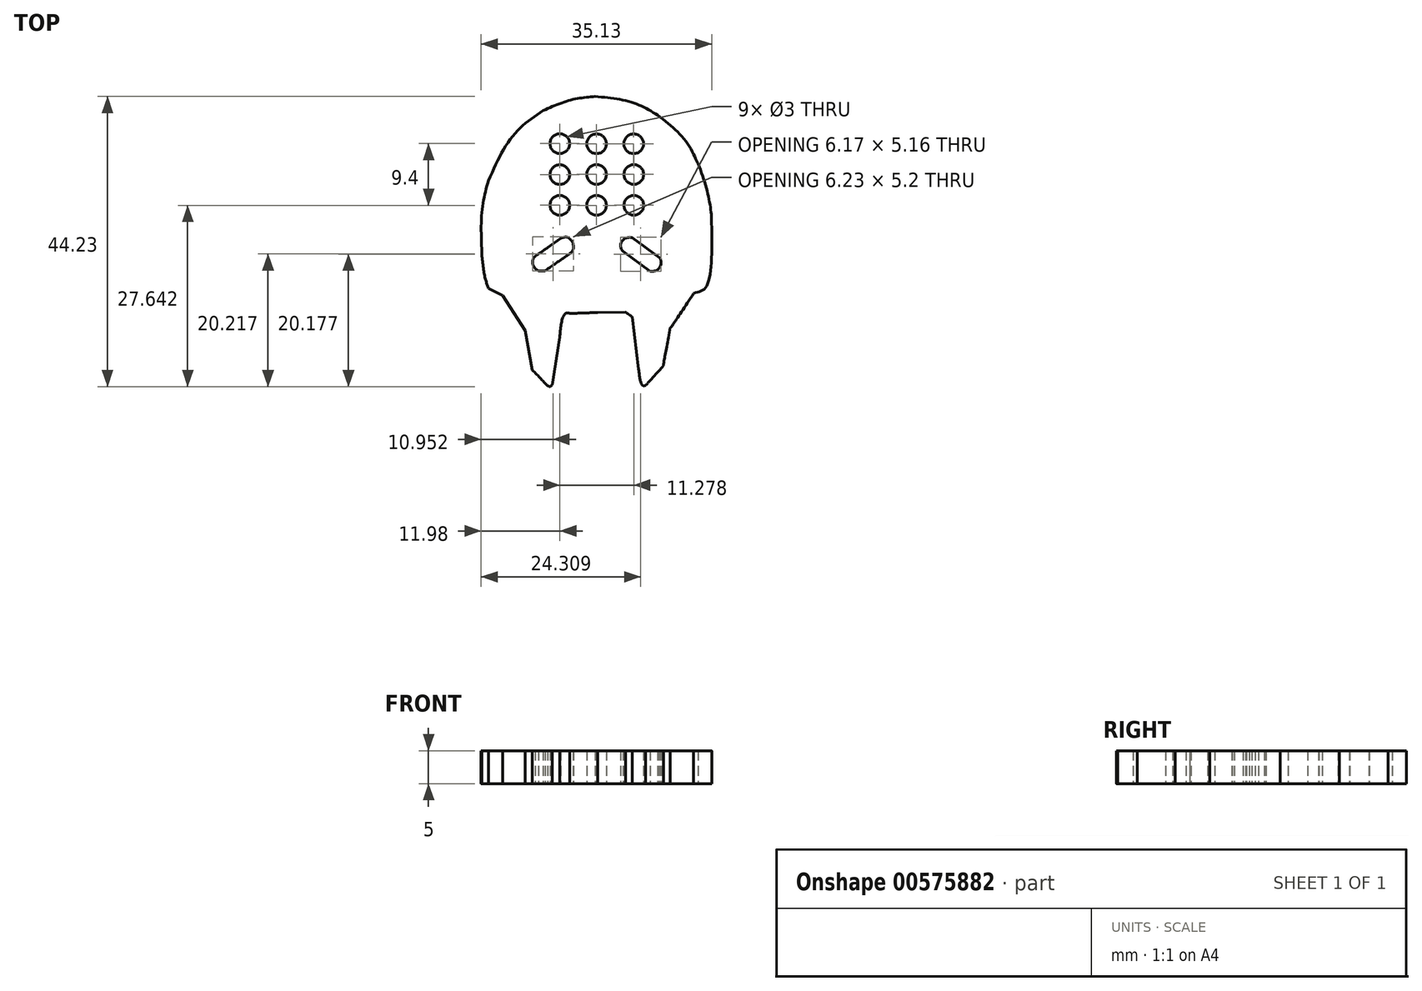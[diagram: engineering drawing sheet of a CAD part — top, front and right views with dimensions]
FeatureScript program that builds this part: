
annotation { "Feature Type Name" : "Feature", "Feature Type Description" : "" }
export const myFeature = defineFeature(function(context is Context, id is Id, definition is map)
    precondition{}
    {
        {
            var Q0;
            Q0=qCreatedBy(makeId("Top.planeOp"),FACE);
            var sketch = newSketch(context, id + "F0", { "sketchPlane" : qUnion([Q0])});
            skFitSpline(sketch, "E0", {"points": [v(28.78, 16.5) * mm, v(24.5, 16.4) * mm], "startDerivative": vector(-4.28, 0) * mm, "endDerivative": vector(-4.28, 0) * mm});
            skFitSpline(sketch, "E1", {"points": [v(24.5, 16.4) * mm, v(23.89, 16.4) * mm, v(23.3, 15.2) * mm, v(22.98, 12.74) * mm], "startDerivative": vector(-3.34, 0.8) * mm, "endDerivative": vector(-0.63, -5.77) * mm});
            skFitSpline(sketch, "E2", {"points": [v(22.98, 12.74) * mm, v(21.82, 5.46) * mm], "startDerivative": vector(-1.15, -7.27) * mm, "endDerivative": vector(-1.15, -7.27) * mm});
            skFitSpline(sketch, "E3", {"points": [v(21.82, 5.46) * mm, v(21.46, 5.22) * mm, v(20.6, 5.93) * mm, v(18.83, 7.75) * mm], "startDerivative": vector(-1.7, -1.87) * mm, "endDerivative": vector(-3.91, 3.94) * mm});
            skFitSpline(sketch, "E4", {"points": [v(18.83, 7.75) * mm, v(17.7, 13.77) * mm], "startDerivative": vector(-1.13, 6.02) * mm, "endDerivative": vector(-1.13, 6.02) * mm});
            skFitSpline(sketch, "E5", {"points": [v(17.7, 13.77) * mm, v(14.28, 19.1) * mm], "startDerivative": vector(-3.42, 5.33) * mm, "endDerivative": vector(-3.42, 5.33) * mm});
            skFitSpline(sketch, "E6", {"points": [v(14.28, 19.1) * mm, v(12.13, 20.22) * mm], "startDerivative": vector(-2.15, 1.12) * mm, "endDerivative": vector(-2.15, 1.12) * mm});
            skFitSpline(sketch, "E7", {"points": [v(12.13, 20.22) * mm, v(11.6, 21.9) * mm, v(11.15, 25.07) * mm], "startDerivative": vector(-1.33, 3.6) * mm, "endDerivative": vector(-0.65, 5.98) * mm});
            skFitSpline(sketch, "E8", {"points": [v(11.15, 25.07) * mm, v(11.15, 32.1) * mm, v(12.13, 36.62) * mm], "startDerivative": vector(-0.6, 13.45) * mm, "endDerivative": vector(2.66, 9.51) * mm});
            skFitSpline(sketch, "E9", {"points": [v(12.13, 36.62) * mm, v(15.93, 43.55) * mm, v(20.45, 47.3) * mm], "startDerivative": vector(6.36, 14.19) * mm, "endDerivative": vector(10.4, 6.99) * mm});
            skFitSpline(sketch, "E10", {"points": [v(20.45, 47.3) * mm, v(24.7, 48.92) * mm, v(28.38, 49.45) * mm], "startDerivative": vector(8.18, 3.62) * mm, "endDerivative": vector(7.66, 0.63) * mm});
            skFitSpline(sketch, "E11", {"points": [v(28.38, 49.45) * mm, v(33.98, 48.57) * mm, v(37.93, 46.6) * mm], "startDerivative": vector(11.1, -0.97) * mm, "endDerivative": vector(7.93, -4.81) * mm});
            skFitSpline(sketch, "E12", {"points": [v(37.93, 46.6) * mm, v(42.66, 42) * mm, v(44.08, 39.22) * mm, v(44.13, 39.22) * mm], "startDerivative": vector(9.54, -7.46) * mm, "endDerivative": vector(0.91, 0.43) * mm});
            skFitSpline(sketch, "E13", {"points": [v(44.08, 39.22) * mm, v(45.88, 33.07) * mm, v(46.13, 30.17) * mm], "startDerivative": vector(4.32, -11.02) * mm, "endDerivative": vector(-0.2, -4) * mm});
            skFitSpline(sketch, "E14", {"points": [v(46.13, 30.17) * mm, v(45.26, 20.37) * mm, v(43.4, 19.44) * mm], "startDerivative": vector(0.3, -18.19) * mm, "endDerivative": vector(-6.92, -2.62) * mm});
            skFitSpline(sketch, "E15", {"points": [v(43.4, 19.44) * mm, v(39.86, 14.17) * mm, v(39.86, 14.2) * mm], "startDerivative": vector(-5.55, -8.44) * mm, "endDerivative": vector(0.11, 0.6) * mm});
            skFitSpline(sketch, "E16", {"points": [v(39.86, 14.2) * mm, v(38.8, 8.42) * mm, v(38.83, 8.44) * mm], "startDerivative": vector(-1.82, -9.27) * mm, "endDerivative": vector(0.4, 0.58) * mm});
            skFitSpline(sketch, "E17", {"points": [v(38.8, 8.42) * mm, v(36.1, 5.42) * mm, v(36.13, 5.44) * mm], "startDerivative": vector(-4.44, -4.91) * mm, "endDerivative": vector(0.43, 0.45) * mm});
            skFitSpline(sketch, "E18", {"points": [v(36.1, 5.42) * mm, v(35.6, 5.42) * mm, v(35.03, 7.87) * mm], "startDerivative": vector(-1.74, -0.55) * mm, "endDerivative": vector(-0.56, 4.77) * mm});
            skFitSpline(sketch, "E19", {"points": [v(35.03, 7.87) * mm, v(34.06, 15.84) * mm], "startDerivative": vector(-0.98, 7.98) * mm, "endDerivative": vector(-0.98, 7.98) * mm});
            skFitSpline(sketch, "E20", {"points": [v(34.06, 15.84) * mm, v(33.03, 16.6) * mm], "startDerivative": vector(-1.05, 0.95) * mm, "endDerivative": vector(-1.05, 0.95) * mm});
            skFitSpline(sketch, "E21", {"points": [v(28.78, 16.5) * mm, v(33.03, 16.6) * mm], "startDerivative": vector(4.25, 0.1) * mm, "endDerivative": vector(4.25, 0.1) * mm});
            skFitSpline(sketch, "E22", {"points": [v(21.16, 26.4) * mm, v(23.13, 27.8) * mm], "startDerivative": vector(1.97, 1.4) * mm, "endDerivative": vector(1.97, 1.4) * mm});
            skFitSpline(sketch, "E23", {"points": [v(23.13, 27.8) * mm, v(23.98, 28.04) * mm, v(24.5, 27.8) * mm], "startDerivative": vector(1.64, 0.7) * mm, "endDerivative": vector(1.07, -0.76) * mm});
            skFitSpline(sketch, "E24", {"points": [v(24.5, 27.8) * mm, v(25, 27.15) * mm, v(25.05, 26.9) * mm], "startDerivative": vector(1.01, -1.1) * mm, "endDerivative": vector(0, -0.62) * mm});
            skFitSpline(sketch, "E25", {"points": [v(25.05, 26.9) * mm, v(25.05, 26.12) * mm, v(24.5, 25.47) * mm], "startDerivative": vector(0.27, -1.7) * mm, "endDerivative": vector(-1.38, -1.07) * mm});
            skFitSpline(sketch, "E26", {"points": [v(24.5, 25.47) * mm, v(20.76, 22.88) * mm], "startDerivative": vector(-3.73, -2.65) * mm, "endDerivative": vector(-3.73, -2.65) * mm});
            skFitSpline(sketch, "E27", {"points": [v(20.76, 22.88) * mm, v(19.8, 22.88) * mm, v(19.28, 23.22) * mm], "startDerivative": vector(-1.9, -0.21) * mm, "endDerivative": vector(-1.03, 0.93) * mm});
            skFitSpline(sketch, "E28", {"points": [v(19.28, 23.22) * mm, v(18.9, 23.87) * mm, v(18.9, 24.52) * mm], "startDerivative": vector(-0.92, 1.24) * mm, "endDerivative": vector(0.18, 1.45) * mm});
            skFitSpline(sketch, "E29", {"points": [v(18.9, 24.52) * mm, v(19.16, 24.97) * mm, v(19.77, 25.47) * mm], "startDerivative": vector(0.2, 1.09) * mm, "endDerivative": vector(1.19, 0.86) * mm});
            skFitSpline(sketch, "E30", {"points": [v(19.77, 25.47) * mm, v(21.16, 26.4) * mm], "startDerivative": vector(1.54, 0.87) * mm, "endDerivative": vector(1.54, 0.87) * mm});
            skFitSpline(sketch, "E31", {"points": [v(34.13, 27.9) * mm, v(38.17, 24.9) * mm], "startDerivative": vector(4.04, -2.99) * mm, "endDerivative": vector(4.04, -2.99) * mm});
            skFitSpline(sketch, "E32", {"points": [v(38.17, 24.9) * mm, v(38.36, 24.6) * mm, v(38.42, 24) * mm, v(38.17, 23.31) * mm, v(37.6, 22.89) * mm, v(36.8, 22.82) * mm], "startDerivative": vector(1.4, -1.8) * mm, "endDerivative": vector(-3.65, 0.07) * mm});
            skFitSpline(sketch, "E33", {"points": [v(36.8, 22.82) * mm, v(32.66, 25.87) * mm], "startDerivative": vector(-4.14, 3.05) * mm, "endDerivative": vector(-4.14, 3.05) * mm});
            skFitSpline(sketch, "E34", {"points": [v(32.66, 25.87) * mm, v(32.31, 26.39) * mm, v(32.26, 26.85) * mm, v(32.53, 27.45) * mm, v(32.92, 27.8) * mm, v(33.5, 27.96) * mm, v(34.13, 27.9) * mm], "startDerivative": vector(-3.62, 3.14) * mm, "endDerivative": vector(3.2, -1.48) * mm});
            skSolve(sketch);
        }
        {
            var Q0;
            Q0=makeQuery(id+"F0.imprint","IMPRINT",FACE,{"disambiguationData":[TD([[makeQuery(id+"F0.imprint","IMPRINT",EDGE,{"derivedFrom":sQuery(id+"F0.wireOp",EDGE,"E0")}),-1.0]])]});
            var sketch = newSketch(context, id + "F1", { "sketchPlane" : qUnion([Q0])});
            skCircle(sketch, "E35", {"center": v(23.01, 32.86) * mm, "radius": 1.5 * mm});
            skCircle(sketch, "E36", {"center": v(-15598.76, 35.03) * mm, "radius": 1.5 * mm});
            skCircle(sketch, "E37", {"center": v(34.29, 32.86) * mm, "radius": 1.5 * mm});
            skCircle(sketch, "E38", {"center": v(23.01, 37.54) * mm, "radius": 1.5 * mm});
            skCircle(sketch, "E39", {"center": v(28.6, 37.56) * mm, "radius": 1.5 * mm});
            skCircle(sketch, "E40", {"center": v(34.29, 37.56) * mm, "radius": 1.5 * mm});
            skCircle(sketch, "E41", {"center": v(23.01, 42.26) * mm, "radius": 1.5 * mm});
            skCircle(sketch, "E42", {"center": v(28.6, 42.24) * mm, "radius": 1.5 * mm});
            skCircle(sketch, "E43", {"center": v(34.27, 42.24) * mm, "radius": 1.5 * mm});
            skCircle(sketch, "E44", {"center": v(28.6, 32.86) * mm, "radius": 1.5 * mm});
            skSolve(sketch);
        }
        {
            var Q0;
            Q0 = qSketchRegion(id + "F0", true);
            extrude(context, id + "F2", {"entities" : qUnion([Q0]), "depth" : 5 * mm, "offsetDistance" : 25 * mm});
        }
        {
            var Q0;
            Q0 = qSketchRegion(id + "F1", true);
            extrude(context, id + "F3", {"entities" : qUnion([Q0]), "operationType" : NewBodyOperationType.REMOVE, "depth" : 5 * mm, "offsetDistance" : 25 * mm});
        }
    });
